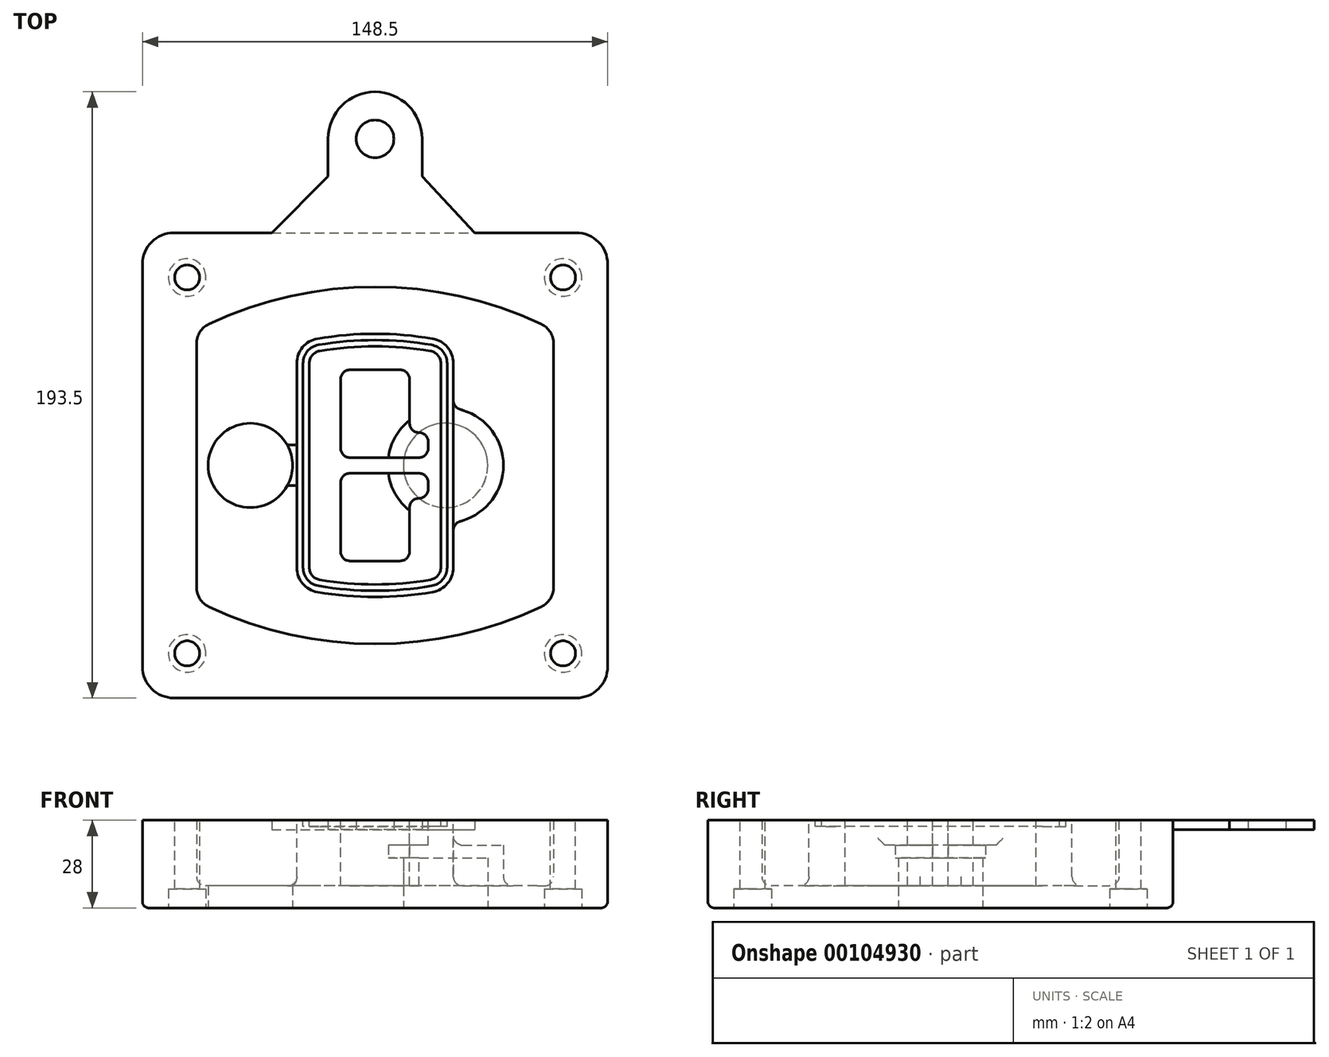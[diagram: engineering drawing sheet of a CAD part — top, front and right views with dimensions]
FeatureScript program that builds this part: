
annotation { "Feature Type Name" : "Feature", "Feature Type Description" : "" }
export const myFeature = defineFeature(function(context is Context, id is Id, definition is map)
    precondition{}
    {
        {
            var Q0;
            Q0=qCreatedBy(makeId("Top.planeOp"),FACE);
            var sketch = newSketch(context, id + "F0", { "sketchPlane" : qUnion([Q0])});
            skPoint(sketch, "E0.rect.middle", {"position": v(0, 0) * mm});
            skLineSegment(sketch, "E1.bottom", {"start": v(-64.25, -74.25) * mm, "end": v(64.25, -74.25) * mm});
            skLineSegment(sketch, "E1.top", {"start": v(-64.25, 74.25) * mm, "end": v(64.25, 74.25) * mm});
            skLineSegment(sketch, "E1.left", {"start": v(-74.25, -64.25) * mm, "end": v(-74.25, 64.25) * mm});
            skLineSegment(sketch, "E1.right", {"start": v(74.25, -64.25) * mm, "end": v(74.25, 64.25) * mm});
            skLineSegment(sketch, "E2", {"start": v(-74.25, 74.25) * mm, "end": v(74.25, -74.25) * mm, "construction": true});
            skLineSegment(sketch, "E3", {"start": v(74.25, 74.25) * mm, "end": v(-74.25, -74.25) * mm, "construction": true});
            skCircle(sketch, "E4", {"center": v(-60, 60) * mm, "radius": 4 * mm});
            skCircle(sketch, "E5", {"center": v(60, 60) * mm, "radius": 4 * mm});
            skCircle(sketch, "E6", {"center": v(60, -60) * mm, "radius": 4 * mm});
            skCircle(sketch, "E7", {"center": v(-60, -60) * mm, "radius": 4 * mm});
            skLineSegment(sketch, "E8", {"start": v(-60, 60) * mm, "end": v(60, 60) * mm, "construction": true});
            skLineSegment(sketch, "E9", {"start": v(60, 60) * mm, "end": v(60, -60) * mm, "construction": true});
            skLineSegment(sketch, "E10", {"start": v(60, -60) * mm, "end": v(-60, -60) * mm, "construction": true});
            skLineSegment(sketch, "E11", {"start": v(-60, -60) * mm, "end": v(-60, 60) * mm, "construction": true});
            skLineSegment(sketch, "E12", {"start": v(-60, 38.83) * mm, "end": v(-60, -38.83) * mm});
            skLineSegment(sketch, "E13", {"start": v(60, 38.83) * mm, "end": v(60, -38.83) * mm});
            skArc(sketch, "E14", {"start": v(54.26, 47.88) * mm, "mid": v(0, 60) * mm, "end": v(-54.26, 47.88) * mm});
            skArc(sketch, "E15", {"start": v(-54.26, -47.88) * mm, "mid": v(0, -60) * mm, "end": v(54.26, -47.88) * mm});
            skLineSegment(sketch, "E16", {"start": v(-60, 0) * mm, "end": v(60, 0) * mm, "construction": true});
            skPoint(sketch, "E17.visualSharp", {"position": v(-60, -45) * mm});
            skArc(sketch, "E17.filletArc", {"start": v(-60, -38.83) * mm, "mid": v(-58.44, -44.2) * mm, "end": v(-54.26, -47.88) * mm});
            skPoint(sketch, "E18.visualSharp", {"position": v(-60, 45) * mm});
            skArc(sketch, "E18.filletArc", {"start": v(-54.26, 47.88) * mm, "mid": v(-58.44, 44.2) * mm, "end": v(-60, 38.83) * mm});
            skPoint(sketch, "E19.visualSharp", {"position": v(60, 45) * mm});
            skArc(sketch, "E19.filletArc", {"start": v(60, 38.83) * mm, "mid": v(58.44, 44.2) * mm, "end": v(54.26, 47.88) * mm});
            skPoint(sketch, "E20.visualSharp", {"position": v(60, -45) * mm});
            skArc(sketch, "E20.filletArc", {"start": v(54.26, -47.88) * mm, "mid": v(58.44, -44.2) * mm, "end": v(60, -38.83) * mm});
            skPoint(sketch, "E21.visualSharp", {"position": v(-74.25, 74.25) * mm});
            skArc(sketch, "E21.filletArc", {"start": v(-64.25, 74.25) * mm, "mid": v(-71.32, 71.32) * mm, "end": v(-74.25, 64.25) * mm});
            skPoint(sketch, "E22.visualSharp", {"position": v(74.25, 74.25) * mm});
            skArc(sketch, "E22.filletArc", {"start": v(74.25, 64.25) * mm, "mid": v(71.32, 71.32) * mm, "end": v(64.25, 74.25) * mm});
            skPoint(sketch, "E23.visualSharp", {"position": v(74.25, -74.25) * mm});
            skArc(sketch, "E23.filletArc", {"start": v(64.25, -74.25) * mm, "mid": v(71.32, -71.32) * mm, "end": v(74.25, -64.25) * mm});
            skPoint(sketch, "E24.visualSharp", {"position": v(-74.25, -74.25) * mm});
            skArc(sketch, "E24.filletArc", {"start": v(-74.25, -64.25) * mm, "mid": v(-71.32, -71.32) * mm, "end": v(-64.25, -74.25) * mm});
            skArc(sketch, "E25.0", {"start": v(57, 38.83) * mm, "mid": v(55.9, 42.58) * mm, "end": v(52.98, 45.17) * mm});
            skLineSegment(sketch, "E25.1", {"start": v(57, 38.83) * mm, "end": v(57, -38.83) * mm});
            skArc(sketch, "E25.2", {"start": v(52.98, -45.17) * mm, "mid": v(55.9, -42.58) * mm, "end": v(57, -38.83) * mm});
            skArc(sketch, "E25.3", {"start": v(-52.98, -45.17) * mm, "mid": v(0, -57) * mm, "end": v(52.98, -45.17) * mm});
            skArc(sketch, "E25.4", {"start": v(-57, -38.83) * mm, "mid": v(-55.9, -42.58) * mm, "end": v(-52.98, -45.17) * mm});
            skArc(sketch, "E25.5", {"start": v(52.98, 45.17) * mm, "mid": v(0, 57) * mm, "end": v(-52.98, 45.17) * mm});
            skLineSegment(sketch, "E25.6", {"start": v(-57, 38.83) * mm, "end": v(-57, -38.83) * mm});
            skArc(sketch, "E25.7", {"start": v(-52.98, 45.17) * mm, "mid": v(-55.9, 42.58) * mm, "end": v(-57, 38.83) * mm});
            skArc(sketch, "E26.0", {"start": v(-55.96, 51.5) * mm, "mid": v(-61.82, 46.33) * mm, "end": v(-64, 38.83) * mm});
            skArc(sketch, "E26.1", {"start": v(55.96, 51.5) * mm, "mid": v(0, 64) * mm, "end": v(-55.96, 51.5) * mm});
            skArc(sketch, "E26.2", {"start": v(64, 38.83) * mm, "mid": v(61.82, 46.33) * mm, "end": v(55.96, 51.5) * mm});
            skLineSegment(sketch, "E26.3", {"start": v(64, 38.83) * mm, "end": v(64, -38.83) * mm});
            skArc(sketch, "E26.4", {"start": v(55.96, -51.5) * mm, "mid": v(61.82, -46.33) * mm, "end": v(64, -38.83) * mm});
            skLineSegment(sketch, "E26.5", {"start": v(-64, 38.83) * mm, "end": v(-64, -38.83) * mm});
            skArc(sketch, "E26.6", {"start": v(-55.96, -51.5) * mm, "mid": v(0, -64) * mm, "end": v(55.96, -51.5) * mm});
            skArc(sketch, "E26.7", {"start": v(-64, -38.83) * mm, "mid": v(-61.82, -46.33) * mm, "end": v(-55.96, -51.5) * mm});
            skSolve(sketch);
        }
        {
            var Q0;
            Q0=makeQuery(id+"F0.imprint","IMPRINT",FACE,{"disambiguationData":[TD([[makeQuery(id+"F0.imprint","IMPRINT",EDGE,{"derivedFrom":sQuery(id+"F0.wireOp",EDGE,"E1.bottom")}),1.0]])]});
            var Q1;
            Q1=makeQuery(id+"F0.imprint","IMPRINT",FACE,{"disambiguationData":[TD([[makeQuery(id+"F0.imprint","IMPRINT",EDGE,{"derivedFrom":sQuery(id+"F0.wireOp",EDGE,"E12")}),1.0]])]});
            var Q2;
            Q2=makeQuery(id+"F0.imprint","IMPRINT",FACE,{"disambiguationData":[TD([[makeQuery(id+"F0.imprint","IMPRINT",EDGE,{"derivedFrom":sQuery(id+"F0.wireOp",EDGE,"E25.0")}),1.0]])]});
            var Q3;
            Q3=makeQuery(id+"F0.imprint","IMPRINT",FACE,{"disambiguationData":[TD([[makeQuery(id+"F0.imprint","IMPRINT",EDGE,{"derivedFrom":sQuery(id+"F0.wireOp",EDGE,"E12")}),-1.0]])]});
            extrude(context, id + "F1", {"entities" : qUnion([Q0, Q1, Q2, Q3]), "oppositeDirection" : true, "depth" : 25 * mm});
        }
        {
            var Q0;
            Q0=makeQuery(id+"F0.imprint","IMPRINT",FACE,{"disambiguationData":[TD([[makeQuery(id+"F0.imprint","IMPRINT",EDGE,{"derivedFrom":sQuery(id+"F0.wireOp",EDGE,"E12")}),1.0]])]});
            extrude(context, id + "F2", {"entities" : qUnion([Q0]), "operationType" : NewBodyOperationType.ADD, "depth" : 3 * mm});
        }
        {
            var Q0;
            Q0=makeQuery(id+"F0.imprint","IMPRINT",FACE,{"disambiguationData":[TD([[makeQuery(id+"F0.imprint","IMPRINT",EDGE,{"derivedFrom":sQuery(id+"F0.wireOp",EDGE,"E25.0")}),1.0]])]});
            extrude(context, id + "F3", {"entities" : qUnion([Q0]), "operationType" : NewBodyOperationType.REMOVE, "oppositeDirection" : true, "depth" : 18 * mm});
        }
        {
            var Q0;
            Q0=makeQuery(id+"F2.opExtrude","CAP_FACE",FACE,{"disambiguationData":[OSD([sQuery(id+"F0.wireOp",EDGE,"E12"),sQuery(id+"F0.wireOp",EDGE,"E13"),sQuery(id+"F0.wireOp",EDGE,"E14"),sQuery(id+"F0.wireOp",EDGE,"E15"),sQuery(id+"F0.wireOp",EDGE,"E17.filletArc"),sQuery(id+"F0.wireOp",EDGE,"E18.filletArc"),sQuery(id+"F0.wireOp",EDGE,"E19.filletArc"),sQuery(id+"F0.wireOp",EDGE,"E20.filletArc"),sQuery(id+"F0.wireOp",EDGE,"E25.0"),sQuery(id+"F0.wireOp",EDGE,"E25.1"),sQuery(id+"F0.wireOp",EDGE,"E25.2"),sQuery(id+"F0.wireOp",EDGE,"E25.3"),sQuery(id+"F0.wireOp",EDGE,"E25.4"),sQuery(id+"F0.wireOp",EDGE,"E25.5"),sQuery(id+"F0.wireOp",EDGE,"E25.6"),sQuery(id+"F0.wireOp",EDGE,"E25.7")])],"isStart":false});
            var sketch = newSketch(context, id + "F4", { "sketchPlane" : qUnion([Q0])});
            skArc(sketch, "E27.0", {"start": v(-18.34, -40.45) * mm, "mid": v(0, -42) * mm, "end": v(18.34, -40.45) * mm});
            skArc(sketch, "E28.0", {"start": v(18.34, 40.45) * mm, "mid": v(0, 42) * mm, "end": v(-18.34, 40.45) * mm});
            skLineSegment(sketch, "E29", {"start": v(-25, 32.57) * mm, "end": v(-25, -32.57) * mm});
            skLineSegment(sketch, "E30", {"start": v(25, 32.57) * mm, "end": v(25, -32.57) * mm});
            skLineSegment(sketch, "E31", {"start": v(-25, 39.1) * mm, "end": v(25, 39.1) * mm, "construction": true});
            skLineSegment(sketch, "E32", {"start": v(-25, -39.1) * mm, "end": v(25, -39.1) * mm, "construction": true});
            skPoint(sketch, "E33.visualSharp", {"position": v(-25, 39.1) * mm});
            skArc(sketch, "E33.filletArc", {"start": v(-18.34, 40.45) * mm, "mid": v(-23.11, 37.73) * mm, "end": v(-25, 32.57) * mm});
            skPoint(sketch, "E34.visualSharp", {"position": v(25, 39.1) * mm});
            skArc(sketch, "E34.filletArc", {"start": v(25, 32.57) * mm, "mid": v(23.11, 37.73) * mm, "end": v(18.34, 40.45) * mm});
            skPoint(sketch, "E35.visualSharp", {"position": v(25, -39.1) * mm});
            skArc(sketch, "E35.filletArc", {"start": v(18.34, -40.45) * mm, "mid": v(23.11, -37.73) * mm, "end": v(25, -32.57) * mm});
            skPoint(sketch, "E36.visualSharp", {"position": v(-25, -39.1) * mm});
            skArc(sketch, "E36.filletArc", {"start": v(-25, -32.57) * mm, "mid": v(-23.11, -37.73) * mm, "end": v(-18.34, -40.45) * mm});
            skArc(sketch, "E37.0", {"start": v(52.98, 45.17) * mm, "mid": v(0, 57) * mm, "end": v(-52.98, 45.17) * mm});
            skArc(sketch, "E37.1", {"start": v(-52.98, 45.17) * mm, "mid": v(-55.9, 42.58) * mm, "end": v(-57, 38.83) * mm});
            skLineSegment(sketch, "E37.2", {"start": v(-57, 38.83) * mm, "end": v(-57, -38.83) * mm});
            skArc(sketch, "E37.3", {"start": v(-57, -38.83) * mm, "mid": v(-55.9, -42.58) * mm, "end": v(-52.98, -45.17) * mm});
            skArc(sketch, "E37.4", {"start": v(-52.98, -45.17) * mm, "mid": v(0, -57) * mm, "end": v(52.98, -45.17) * mm});
            skArc(sketch, "E37.5", {"start": v(52.98, -45.17) * mm, "mid": v(55.9, -42.58) * mm, "end": v(57, -38.83) * mm});
            skLineSegment(sketch, "E37.6", {"start": v(57, 38.83) * mm, "end": v(57, -38.83) * mm});
            skArc(sketch, "E37.7", {"start": v(57, 38.83) * mm, "mid": v(55.9, 42.58) * mm, "end": v(52.98, 45.17) * mm});
            skLineSegment(sketch, "E38.0", {"start": v(23, 32.57) * mm, "end": v(23, -32.57) * mm});
            skArc(sketch, "E38.1", {"start": v(18, -38.48) * mm, "mid": v(21.58, -36.44) * mm, "end": v(23, -32.57) * mm});
            skArc(sketch, "E38.2", {"start": v(-18, -38.48) * mm, "mid": v(0, -40) * mm, "end": v(18, -38.48) * mm});
            skArc(sketch, "E38.3", {"start": v(-23, -32.57) * mm, "mid": v(-21.58, -36.44) * mm, "end": v(-18, -38.48) * mm});
            skLineSegment(sketch, "E38.4", {"start": v(-23, 32.57) * mm, "end": v(-23, -32.57) * mm});
            skArc(sketch, "E38.5", {"start": v(23, 32.57) * mm, "mid": v(21.58, 36.44) * mm, "end": v(18, 38.48) * mm});
            skArc(sketch, "E38.6", {"start": v(-18, 38.48) * mm, "mid": v(-21.58, 36.44) * mm, "end": v(-23, 32.57) * mm});
            skArc(sketch, "E38.7", {"start": v(18, 38.48) * mm, "mid": v(0, 40) * mm, "end": v(-18, 38.48) * mm});
            skArc(sketch, "E39.0", {"start": v(21, 32.57) * mm, "mid": v(20.06, 35.15) * mm, "end": v(17.67, 36.5) * mm});
            skLineSegment(sketch, "E39.1", {"start": v(21, 32.57) * mm, "end": v(21, -32.57) * mm});
            skArc(sketch, "E39.2", {"start": v(17.67, -36.5) * mm, "mid": v(20.06, -35.15) * mm, "end": v(21, -32.57) * mm});
            skArc(sketch, "E39.3", {"start": v(-17.67, -36.5) * mm, "mid": v(0, -38) * mm, "end": v(17.67, -36.5) * mm});
            skArc(sketch, "E39.4", {"start": v(-21, -32.57) * mm, "mid": v(-20.06, -35.15) * mm, "end": v(-17.67, -36.5) * mm});
            skArc(sketch, "E39.5", {"start": v(17.67, 36.5) * mm, "mid": v(0, 38) * mm, "end": v(-17.67, 36.5) * mm});
            skLineSegment(sketch, "E39.6", {"start": v(-21, 32.57) * mm, "end": v(-21, -32.57) * mm});
            skArc(sketch, "E39.7", {"start": v(-17.67, 36.5) * mm, "mid": v(-20.06, 35.15) * mm, "end": v(-21, 32.57) * mm});
            skLineSegment(sketch, "E40", {"start": v(-25, 0) * mm, "end": v(25, 0) * mm, "construction": true});
            skLineSegment(sketch, "E41", {"start": v(-11, 5.5) * mm, "end": v(-11, 27.5) * mm});
            skLineSegment(sketch, "E42", {"start": v(-8, 30.5) * mm, "end": v(8, 30.5) * mm});
            skLineSegment(sketch, "E43", {"start": v(11, 27.5) * mm, "end": v(11, 13.5) * mm});
            skLineSegment(sketch, "E44", {"start": v(14, 10.5) * mm, "end": v(14, 10.5) * mm});
            skLineSegment(sketch, "E45", {"start": v(17, 7.5) * mm, "end": v(17, 5.5) * mm});
            skLineSegment(sketch, "E46", {"start": v(14, 2.5) * mm, "end": v(-8, 2.5) * mm});
            skPoint(sketch, "E47.visualSharp", {"position": v(-11, 30.5) * mm});
            skArc(sketch, "E47.filletArc", {"start": v(-8, 30.5) * mm, "mid": v(-10.12, 29.62) * mm, "end": v(-11, 27.5) * mm});
            skPoint(sketch, "E48.visualSharp", {"position": v(11, 30.5) * mm});
            skArc(sketch, "E48.filletArc", {"start": v(11, 27.5) * mm, "mid": v(10.12, 29.62) * mm, "end": v(8, 30.5) * mm});
            skPoint(sketch, "E49.visualSharp", {"position": v(11, 10.5) * mm});
            skArc(sketch, "E49.filletArc", {"start": v(11, 13.5) * mm, "mid": v(11.88, 11.38) * mm, "end": v(14, 10.5) * mm});
            skPoint(sketch, "E50.visualSharp", {"position": v(17, 10.5) * mm});
            skArc(sketch, "E50.filletArc", {"start": v(17, 7.5) * mm, "mid": v(16.12, 9.62) * mm, "end": v(14, 10.5) * mm});
            skPoint(sketch, "E51.visualSharp", {"position": v(17, 2.5) * mm});
            skArc(sketch, "E51.filletArc", {"start": v(14, 2.5) * mm, "mid": v(16.12, 3.38) * mm, "end": v(17, 5.5) * mm});
            skPoint(sketch, "E52.visualSharp", {"position": v(-11, 2.5) * mm});
            skArc(sketch, "E52.filletArc", {"start": v(-11, 5.5) * mm, "mid": v(-10.12, 3.38) * mm, "end": v(-8, 2.5) * mm});
            skLineSegment(sketch, "E53.0.MirrorCS", {"start": v(14, -2.5) * mm, "end": v(-8, -2.5) * mm});
            skArc(sketch, "E54.0.MirrorCS", {"start": v(-11, -5.5) * mm, "mid": v(-10.12, -3.38) * mm, "end": v(-8, -2.5) * mm});
            skLineSegment(sketch, "E55.0.MirrorCS", {"start": v(-11, -5.5) * mm, "end": v(-11, -27.5) * mm});
            skArc(sketch, "E56.0.MirrorCS", {"start": v(-8, -30.5) * mm, "mid": v(-10.12, -29.62) * mm, "end": v(-11, -27.5) * mm});
            skLineSegment(sketch, "E57.0.MirrorCS", {"start": v(-8, -30.5) * mm, "end": v(8, -30.5) * mm});
            skArc(sketch, "E58.0.MirrorCS", {"start": v(11, -27.5) * mm, "mid": v(10.12, -29.62) * mm, "end": v(8, -30.5) * mm});
            skLineSegment(sketch, "E59.0.MirrorCS", {"start": v(11, -27.5) * mm, "end": v(11, -13.5) * mm});
            skArc(sketch, "E60.0.MirrorCS", {"start": v(11, -13.5) * mm, "mid": v(11.88, -11.38) * mm, "end": v(14, -10.5) * mm});
            skArc(sketch, "E61.0.MirrorCS", {"start": v(17, -7.5) * mm, "mid": v(16.12, -9.62) * mm, "end": v(14, -10.5) * mm});
            skLineSegment(sketch, "E62.0.MirrorCS", {"start": v(17, -7.5) * mm, "end": v(17, -5.5) * mm});
            skArc(sketch, "E63.0.MirrorCS", {"start": v(14, -2.5) * mm, "mid": v(16.12, -3.38) * mm, "end": v(17, -5.5) * mm});
            skSolve(sketch);
        }
        {
            var Q0;
            Q0=makeQuery(id+"F4.imprint","IMPRINT",FACE,{"disambiguationData":[TD([[makeQuery(id+"F4.imprint","IMPRINT",EDGE,{"derivedFrom":sQuery(id+"F4.wireOp",EDGE,"E27.0")}),1.0]])]});
            var Q1;
            Q1=makeQuery(id+"F4.imprint","IMPRINT",FACE,{"disambiguationData":[TD([[makeQuery(id+"F4.imprint","IMPRINT",EDGE,{"derivedFrom":sQuery(id+"F4.wireOp",EDGE,"E38.0")}),-1.0]])]});
            var Q2;
            Q2=makeQuery(id+"F4.imprint","IMPRINT",FACE,{"disambiguationData":[TD([[makeQuery(id+"F4.imprint","IMPRINT",EDGE,{"derivedFrom":sQuery(id+"F4.wireOp",EDGE,"E39.0")}),1.0]])]});
            extrude(context, id + "F5", {"entities" : qUnion([Q0, Q1, Q2]), "operationType" : NewBodyOperationType.ADD, "endBound" : BoundingType.UP_TO_NEXT, "oppositeDirection" : true, "depth" : 25 * mm});
        }
        {
            var Q0;
            Q0=makeQuery(id+"F4.imprint","IMPRINT",FACE,{"disambiguationData":[TD([[makeQuery(id+"F4.imprint","IMPRINT",EDGE,{"derivedFrom":sQuery(id+"F4.wireOp",EDGE,"E38.0")}),-1.0]])]});
            extrude(context, id + "F6", {"entities" : qUnion([Q0]), "operationType" : NewBodyOperationType.REMOVE, "oppositeDirection" : true, "depth" : 2 * mm});
        }
        {
            var Q0;
            Q0=makeQuery(id+"F1.opExtrude","CAP_FACE",FACE,{"disambiguationData":[OSD([sQuery(id+"F0.wireOp",EDGE,"E1.bottom"),sQuery(id+"F0.wireOp",EDGE,"E1.top"),sQuery(id+"F0.wireOp",EDGE,"E1.left"),sQuery(id+"F0.wireOp",EDGE,"E1.right"),sQuery(id+"F0.wireOp",EDGE,"E4"),sQuery(id+"F0.wireOp",EDGE,"E5"),sQuery(id+"F0.wireOp",EDGE,"E6"),sQuery(id+"F0.wireOp",EDGE,"E7"),sQuery(id+"F0.wireOp",EDGE,"E21.filletArc"),sQuery(id+"F0.wireOp",EDGE,"E22.filletArc"),sQuery(id+"F0.wireOp",EDGE,"E23.filletArc"),sQuery(id+"F0.wireOp",EDGE,"E24.filletArc")])],"isStart":false});
            var sketch = newSketch(context, id + "F7", { "sketchPlane" : qUnion([Q0])});
            skCircle(sketch, "E64", {"center": v(22.5, 0) * mm, "radius": 13.47 * mm});
            skCircle(sketch, "E65", {"center": v(-39.81, 0) * mm, "radius": 13.47 * mm});
            skLineSegment(sketch, "E66", {"start": v(74.25, 0) * mm, "end": v(-74.25, 0) * mm});
            skCircle(sketch, "E67", {"center": v(22.5, 0) * mm, "radius": 18.47 * mm});
            skCircle(sketch, "E68", {"center": v(60, -60) * mm, "radius": 6 * mm});
            skCircle(sketch, "E69", {"center": v(-60, -60) * mm, "radius": 6 * mm});
            skCircle(sketch, "E70", {"center": v(-60, 60) * mm, "radius": 6 * mm});
            skCircle(sketch, "E71", {"center": v(60, 60) * mm, "radius": 6 * mm});
            skSolve(sketch);
        }
        {
            var Q0;
            {var subQ1=sQuery(id+"F7.wireOp",EDGE,"E66");var subQ4=sQuery(id+"F7.wireOp",EDGE,"E64");var subQ6=makeQuery(id+"F7.imprint","INTERSECT",VERTEX,{"disambiguationData":[OD(0.0)],"derivedFrom":[subQ4,subQ1]});Q0=makeQuery(id+"F7.imprint","IMPRINT",FACE,{"disambiguationData":[TD([[makeQuery(id+"F7.imprint","IMPRINT",EDGE,{"disambiguationData":[TD([[subQ6,-1.0]])],"derivedFrom":subQ4}),-1.0]])]});}
            var Q1;
            {var subQ0=sQuery(id+"F7.wireOp",EDGE,"E66");var subQ1=sQuery(id+"F7.wireOp",EDGE,"E64");var subQ3=makeQuery(id+"F7.imprint","INTERSECT",VERTEX,{"disambiguationData":[OD(0.0)],"derivedFrom":[subQ1,subQ0]});Q1=makeQuery(id+"F7.imprint","IMPRINT",FACE,{"disambiguationData":[TD([[makeQuery(id+"F7.imprint","IMPRINT",EDGE,{"disambiguationData":[TD([[subQ3,-1.0]])],"derivedFrom":subQ1}),1.0]])]});}
            var Q2;
            {var subQ0=sQuery(id+"F7.wireOp",EDGE,"E66");var subQ1=sQuery(id+"F7.wireOp",EDGE,"E64");var subQ3=makeQuery(id+"F7.imprint","INTERSECT",VERTEX,{"disambiguationData":[OD(0.0)],"derivedFrom":[subQ1,subQ0]});Q2=makeQuery(id+"F7.imprint","IMPRINT",FACE,{"disambiguationData":[TD([[makeQuery(id+"F7.imprint","IMPRINT",EDGE,{"disambiguationData":[TD([[subQ3,1.0]])],"derivedFrom":subQ1}),1.0]])]});}
            var Q3;
            {var subQ1=sQuery(id+"F7.wireOp",EDGE,"E66");var subQ4=sQuery(id+"F7.wireOp",EDGE,"E64");var subQ6=makeQuery(id+"F7.imprint","INTERSECT",VERTEX,{"disambiguationData":[OD(0.0)],"derivedFrom":[subQ4,subQ1]});Q3=makeQuery(id+"F7.imprint","IMPRINT",FACE,{"disambiguationData":[TD([[makeQuery(id+"F7.imprint","IMPRINT",EDGE,{"disambiguationData":[TD([[subQ6,1.0]])],"derivedFrom":subQ4}),-1.0]])]});}
            extrude(context, id + "F8", {"entities" : qUnion([Q0, Q1, Q2, Q3]), "operationType" : NewBodyOperationType.ADD, "oppositeDirection" : true, "depth" : 20 * mm});
        }
        {
            var Q0;
            {var subQ0=sQuery(id+"F7.wireOp",EDGE,"E66");var subQ1=sQuery(id+"F7.wireOp",EDGE,"E64");var subQ3=makeQuery(id+"F7.imprint","INTERSECT",VERTEX,{"disambiguationData":[OD(0.0)],"derivedFrom":[subQ1,subQ0]});Q0=makeQuery(id+"F7.imprint","IMPRINT",FACE,{"disambiguationData":[TD([[makeQuery(id+"F7.imprint","IMPRINT",EDGE,{"disambiguationData":[TD([[subQ3,-1.0]])],"derivedFrom":subQ1}),1.0]])]});}
            var Q1;
            {var subQ0=sQuery(id+"F7.wireOp",EDGE,"E66");var subQ1=sQuery(id+"F7.wireOp",EDGE,"E64");var subQ3=makeQuery(id+"F7.imprint","INTERSECT",VERTEX,{"disambiguationData":[OD(0.0)],"derivedFrom":[subQ1,subQ0]});Q1=makeQuery(id+"F7.imprint","IMPRINT",FACE,{"disambiguationData":[TD([[makeQuery(id+"F7.imprint","IMPRINT",EDGE,{"disambiguationData":[TD([[subQ3,1.0]])],"derivedFrom":subQ1}),1.0]])]});}
            extrude(context, id + "F9", {"entities" : qUnion([Q0, Q1]), "operationType" : NewBodyOperationType.REMOVE, "oppositeDirection" : true, "depth" : 16 * mm});
        }
        {
            var Q0;
            {var subQ0=sQuery(id+"F7.wireOp",EDGE,"E66");var subQ1=sQuery(id+"F7.wireOp",EDGE,"E65");var subQ3=makeQuery(id+"F7.imprint","INTERSECT",VERTEX,{"disambiguationData":[OD(0.0)],"derivedFrom":[subQ1,subQ0]});Q0=makeQuery(id+"F7.imprint","IMPRINT",FACE,{"disambiguationData":[TD([[makeQuery(id+"F7.imprint","IMPRINT",EDGE,{"disambiguationData":[TD([[subQ3,-1.0]])],"derivedFrom":subQ1}),1.0]])]});}
            var Q1;
            {var subQ0=sQuery(id+"F7.wireOp",EDGE,"E66");var subQ1=sQuery(id+"F7.wireOp",EDGE,"E65");var subQ3=makeQuery(id+"F7.imprint","INTERSECT",VERTEX,{"disambiguationData":[OD(0.0)],"derivedFrom":[subQ1,subQ0]});Q1=makeQuery(id+"F7.imprint","IMPRINT",FACE,{"disambiguationData":[TD([[makeQuery(id+"F7.imprint","IMPRINT",EDGE,{"disambiguationData":[TD([[subQ3,1.0]])],"derivedFrom":subQ1}),1.0]])]});}
            extrude(context, id + "F10", {"entities" : qUnion([Q0, Q1]), "operationType" : NewBodyOperationType.REMOVE, "oppositeDirection" : true, "depth" : 25 * mm});
        }
        {
            var Q0;
            Q0=makeQuery(id+"F7.imprint","IMPRINT",FACE,{"disambiguationData":[TD([[makeQuery(id+"F7.imprint","IMPRINT",EDGE,{"derivedFrom":sQuery(id+"F7.wireOp",EDGE,"E68")}),1.0]])]});
            var Q1;
            Q1=makeQuery(id+"F7.imprint","IMPRINT",FACE,{"disambiguationData":[TD([[makeQuery(id+"F7.imprint","IMPRINT",EDGE,{"derivedFrom":makeQuery(id+"F1.opExtrude","CAP_EDGE",EDGE,{"disambiguationData":[OSD([sQuery(id+"F0.wireOp",EDGE,"E5")])],"isStart":false})}),-1.0]])]});
            var Q2;
            Q2=makeQuery(id+"F7.imprint","IMPRINT",FACE,{"disambiguationData":[TD([[makeQuery(id+"F7.imprint","IMPRINT",EDGE,{"derivedFrom":sQuery(id+"F7.wireOp",EDGE,"E69")}),1.0]])]});
            var Q3;
            Q3=makeQuery(id+"F7.imprint","IMPRINT",FACE,{"disambiguationData":[TD([[makeQuery(id+"F7.imprint","IMPRINT",EDGE,{"derivedFrom":makeQuery(id+"F1.opExtrude","CAP_EDGE",EDGE,{"disambiguationData":[OSD([sQuery(id+"F0.wireOp",EDGE,"E4")])],"isStart":false})}),-1.0]])]});
            var Q4;
            Q4=makeQuery(id+"F7.imprint","IMPRINT",FACE,{"disambiguationData":[TD([[makeQuery(id+"F7.imprint","IMPRINT",EDGE,{"derivedFrom":sQuery(id+"F7.wireOp",EDGE,"E70")}),1.0]])]});
            var Q5;
            Q5=makeQuery(id+"F7.imprint","IMPRINT",FACE,{"disambiguationData":[TD([[makeQuery(id+"F7.imprint","IMPRINT",EDGE,{"derivedFrom":makeQuery(id+"F1.opExtrude","CAP_EDGE",EDGE,{"disambiguationData":[OSD([sQuery(id+"F0.wireOp",EDGE,"E7")])],"isStart":false})}),-1.0]])]});
            var Q6;
            Q6=makeQuery(id+"F7.imprint","IMPRINT",FACE,{"disambiguationData":[TD([[makeQuery(id+"F7.imprint","IMPRINT",EDGE,{"derivedFrom":sQuery(id+"F7.wireOp",EDGE,"E71")}),1.0]])]});
            var Q7;
            Q7=makeQuery(id+"F7.imprint","IMPRINT",FACE,{"disambiguationData":[TD([[makeQuery(id+"F7.imprint","IMPRINT",EDGE,{"derivedFrom":makeQuery(id+"F1.opExtrude","CAP_EDGE",EDGE,{"disambiguationData":[OSD([sQuery(id+"F0.wireOp",EDGE,"E6")])],"isStart":false})}),-1.0]])]});
            extrude(context, id + "F11", {"entities" : qUnion([Q0, Q1, Q2, Q3, Q4, Q5, Q6, Q7]), "operationType" : NewBodyOperationType.REMOVE, "oppositeDirection" : true, "depth" : 6 * mm});
        }
        {
            var Q0;
            Q0=makeQuery(id+"F9.boolean.opBoolean","COPY",FACE,{"derivedFrom":makeQuery(id+"F9.opExtrude","CAP_FACE",FACE,{"disambiguationData":[OSD([sQuery(id+"F7.wireOp",EDGE,"E64")])],"isStart":false})});
            var sketch = newSketch(context, id + "F12", { "sketchPlane" : qUnion([Q0])});
            skArc(sketch, "E72.0", {"start": v(11, 14.45) * mm, "mid": v(6.45, 9.13) * mm, "end": v(4.2, 2.5) * mm});
            skArc(sketch, "E72.1", {"start": v(4.2, -2.5) * mm, "mid": v(6.45, -9.13) * mm, "end": v(11, -14.45) * mm});
            skLineSegment(sketch, "E73", {"start": v(4.2, -2.5) * mm, "end": v(14, -2.5) * mm});
            skLineSegment(sketch, "E74.0", {"start": v(14, 2.5) * mm, "end": v(4.2, 2.5) * mm});
            skArc(sketch, "E74.1", {"start": v(14, 2.5) * mm, "mid": v(16.12, 3.38) * mm, "end": v(17, 5.5) * mm});
            skLineSegment(sketch, "E74.2", {"start": v(17, 7.5) * mm, "end": v(17, 5.5) * mm});
            skArc(sketch, "E74.3", {"start": v(17, 7.5) * mm, "mid": v(16.12, 9.62) * mm, "end": v(14, 10.5) * mm});
            skArc(sketch, "E74.4", {"start": v(11, 13.5) * mm, "mid": v(11.88, 11.38) * mm, "end": v(14, 10.5) * mm});
            skLineSegment(sketch, "E74.5", {"start": v(11, 14.45) * mm, "end": v(11, 13.5) * mm});
            skLineSegment(sketch, "E74.7", {"start": v(14, -2.5) * mm, "end": v(4.2, -2.5) * mm});
            skArc(sketch, "E74.8", {"start": v(14, -2.5) * mm, "mid": v(16.12, -3.38) * mm, "end": v(17, -5.5) * mm});
            skLineSegment(sketch, "E74.9", {"start": v(17, -7.5) * mm, "end": v(17, -5.5) * mm});
            skArc(sketch, "E74.10", {"start": v(17, -7.5) * mm, "mid": v(16.12, -9.62) * mm, "end": v(14, -10.5) * mm});
            skArc(sketch, "E74.11", {"start": v(11, -13.5) * mm, "mid": v(11.88, -11.38) * mm, "end": v(14, -10.5) * mm});
            skLineSegment(sketch, "E74.12", {"start": v(11, -14.45) * mm, "end": v(11, -13.5) * mm});
            skPoint(sketch, "E75.orphan", {"position": v(11, -27.5) * mm});
            skPoint(sketch, "E76.orphan", {"position": v(-8, -2.5) * mm});
            skPoint(sketch, "E77.orphan", {"position": v(-8, 2.5) * mm});
            skPoint(sketch, "E78.orphan", {"position": v(11, 27.5) * mm});
            skSolve(sketch);
        }
        {
            var Q0;
            {var subQ7=sQuery(id+"F12.wireOp",EDGE,"E72.0");var subQ14=sQuery(id+"F12.wireOp",EDGE,"E72.1");var subQ16=sQuery(id+"F12.wireOp",EDGE,"E74.1");var subQ18=sQuery(id+"F12.wireOp",EDGE,"E74.8");Q0=qUnion([makeQuery(id+"F12.imprint","IMPRINT",FACE,{"disambiguationData":[TD([[makeQuery(id+"F12.imprint","IMPRINT",EDGE,{"derivedFrom":subQ7}),1.0]])]}),makeQuery(id+"F12.imprint","IMPRINT",FACE,{"disambiguationData":[TD([[makeQuery(id+"F12.imprint","IMPRINT",EDGE,{"derivedFrom":subQ14}),1.0]])]}),makeQuery(id+"F12.imprint","IMPRINT",FACE,{"disambiguationData":[TD([[makeQuery(id+"F12.imprint","IMPRINT",EDGE,{"derivedFrom":subQ16}),1.0]])]}),makeQuery(id+"F12.imprint","IMPRINT",FACE,{"disambiguationData":[TD([[makeQuery(id+"F12.imprint","IMPRINT",EDGE,{"derivedFrom":subQ18}),-1.0]])]})]);}
            var Q1;
            Q1=makeQuery(id+"F5.boolean.opBoolean","SPLIT",FACE,{"disambiguationData":[TD([makeQuery(id+"F5.opExtrude","SWEPT_FACE",FACE,{"disambiguationData":[OSD([sQuery(id+"F4.wireOp",EDGE,"E41")])]})])],"derivedFrom":makeQuery(id+"F3.boolean.opBoolean","COPY",FACE,{"derivedFrom":makeQuery(id+"F3.opExtrude","CAP_FACE",FACE,{"disambiguationData":[OSD([sQuery(id+"F0.wireOp",EDGE,"E25.0"),sQuery(id+"F0.wireOp",EDGE,"E25.1"),sQuery(id+"F0.wireOp",EDGE,"E25.2"),sQuery(id+"F0.wireOp",EDGE,"E25.3"),sQuery(id+"F0.wireOp",EDGE,"E25.4"),sQuery(id+"F0.wireOp",EDGE,"E25.5"),sQuery(id+"F0.wireOp",EDGE,"E25.6"),sQuery(id+"F0.wireOp",EDGE,"E25.7")])],"isStart":false})})});
            extrude(context, id + "F13", {"entities" : qUnion([Q0]), "operationType" : NewBodyOperationType.REMOVE, "endBound" : BoundingType.UP_TO_SURFACE, "endBoundEntityFace" : qUnion([Q1]), "depth" : 25 * mm});
        }
        {
            var Q0;
            Q0=makeQuery(id+"F3.boolean.opBoolean","COPY",EDGE,{"derivedFrom":makeQuery(id+"F3.opExtrude","CAP_EDGE",EDGE,{"disambiguationData":[OSD([sQuery(id+"F0.wireOp",EDGE,"E25.6")])],"isStart":false})});
            var Q1;
            Q1=makeQuery(id+"F8.boolean.opBoolean","INTERSECT",EDGE,{"derivedFrom":[makeQuery(id+"F5.opExtrude","SWEPT_FACE",FACE,{"disambiguationData":[OSD([sQuery(id+"F4.wireOp",EDGE,"E30")])]}),makeQuery(id+"F8.opExtrude","CAP_FACE",FACE,{"disambiguationData":[OSD([sQuery(id+"F7.wireOp",EDGE,"E67")])],"isStart":false})]});
            var Q2;
            Q2=makeQuery(id+"F8.boolean.opBoolean","INTERSECT",EDGE,{"disambiguationData":[OD(1.0)],"derivedFrom":[makeQuery(id+"F5.opExtrude","SWEPT_FACE",FACE,{"disambiguationData":[OSD([sQuery(id+"F4.wireOp",EDGE,"E30")])]}),makeQuery(id+"F8.opExtrude","SWEPT_FACE",FACE,{"disambiguationData":[OSD([sQuery(id+"F7.wireOp",EDGE,"E67")])]})]});
            var Q3;
            {var subQ0=sQuery(id+"F4.wireOp",EDGE,"E30");Q3=makeQuery(id+"F8.boolean.opBoolean","SPLIT",EDGE,{"disambiguationData":[TD([makeQuery(id+"F5.opExtrude","SWEPT_FACE",FACE,{"disambiguationData":[OSD([sQuery(id+"F4.wireOp",EDGE,"E35.filletArc")])]})])],"derivedFrom":makeQuery(id+"F5.opExtrude","CAP_EDGE",EDGE,{"disambiguationData":[OSD([subQ0])],"isStart":false})});}
            var Q4;
            {var subQ0=sQuery(id+"F0.wireOp",EDGE,"E25.7");var subQ1=sQuery(id+"F0.wireOp",EDGE,"E25.1");var subQ2=sQuery(id+"F0.wireOp",EDGE,"E25.6");var subQ3=sQuery(id+"F0.wireOp",EDGE,"E25.5");var subQ4=sQuery(id+"F0.wireOp",EDGE,"E25.4");var subQ5=sQuery(id+"F0.wireOp",EDGE,"E25.0");var subQ6=sQuery(id+"F0.wireOp",EDGE,"E25.2");var subQ7=sQuery(id+"F0.wireOp",EDGE,"E25.3");Q4=makeQuery(id+"F8.boolean.opBoolean","INTERSECT",EDGE,{"derivedFrom":[makeQuery(id+"F5.boolean.opBoolean","SPLIT",FACE,{"disambiguationData":[TD([makeQuery(id+"F2.opExtrude","SWEPT_FACE",FACE,{"disambiguationData":[OSD([subQ5])]})])],"derivedFrom":makeQuery(id+"F3.boolean.opBoolean","COPY",FACE,{"derivedFrom":makeQuery(id+"F3.opExtrude","CAP_FACE",FACE,{"disambiguationData":[OSD([subQ5,subQ1,subQ6,subQ7,subQ4,subQ3,subQ2,subQ0])],"isStart":false})})}),makeQuery(id+"F8.opExtrude","SWEPT_FACE",FACE,{"disambiguationData":[OSD([sQuery(id+"F7.wireOp",EDGE,"E67")])]})]});}
            var Q5;
            Q5=makeQuery(id+"F8.boolean.opBoolean","INTERSECT",EDGE,{"disambiguationData":[OD(0.0)],"derivedFrom":[makeQuery(id+"F5.opExtrude","SWEPT_FACE",FACE,{"disambiguationData":[OSD([sQuery(id+"F4.wireOp",EDGE,"E30")])]}),makeQuery(id+"F8.opExtrude","SWEPT_FACE",FACE,{"disambiguationData":[OSD([sQuery(id+"F7.wireOp",EDGE,"E67")])]})]});
            fillet(context, id + "F14", {"entities" : qUnion([Q0, Q1, Q2, Q3, Q4, Q5]), "radius" : 3 * mm, "tangentPropagation" : true, "allowEdgeOverflow" : false});
        }
        {
            var Q0;
            Q0=makeQuery(id+"F1.opExtrude","CAP_EDGE",EDGE,{"disambiguationData":[OSD([sQuery(id+"F0.wireOp",EDGE,"E1.bottom")])],"isStart":false});
            fillet(context, id + "F15", {"entities" : qUnion([Q0]), "radius" : 2 * mm, "tangentPropagation" : true, "allowEdgeOverflow" : false});
        }
        {
            var Q0;
            {var subQ0=sQuery(id+"F0.wireOp",EDGE,"E22.filletArc");var subQ1=sQuery(id+"F0.wireOp",EDGE,"E7");var subQ2=sQuery(id+"F0.wireOp",EDGE,"E6");var subQ3=sQuery(id+"F0.wireOp",EDGE,"E5");var subQ4=sQuery(id+"F0.wireOp",EDGE,"E4");var subQ5=sQuery(id+"F0.wireOp",EDGE,"E1.bottom");var subQ6=sQuery(id+"F0.wireOp",EDGE,"E21.filletArc");var subQ7=sQuery(id+"F0.wireOp",EDGE,"E1.top");var subQ8=sQuery(id+"F0.wireOp",EDGE,"E1.left");var subQ9=sQuery(id+"F0.wireOp",EDGE,"E1.right");var subQ10=sQuery(id+"F0.wireOp",EDGE,"E23.filletArc");var subQ11=sQuery(id+"F0.wireOp",EDGE,"E24.filletArc");Q0=makeQuery(id+"F2.boolean.opBoolean","SPLIT",FACE,{"disambiguationData":[TD([makeQuery(id+"F1.opExtrude","SWEPT_FACE",FACE,{"disambiguationData":[OSD([subQ5])]})])],"derivedFrom":makeQuery(id+"F1.opExtrude","CAP_FACE",FACE,{"disambiguationData":[OSD([subQ5,subQ7,subQ8,subQ9,subQ4,subQ3,subQ2,subQ1,subQ6,subQ0,subQ10,subQ11])],"isStart":true})});}
            var sketch = newSketch(context, id + "F16", { "sketchPlane" : qUnion([Q0])});
            skLineSegment(sketch, "E79", {"start": v(0, 74.25) * mm, "end": v(0, 104.25) * mm, "construction": true});
            skLineSegment(sketch, "E80", {"start": v(-33, 74.25) * mm, "end": v(-15, 92.25) * mm});
            skLineSegment(sketch, "E81", {"start": v(15, 92.25) * mm, "end": v(31.77, 74.25) * mm});
            skCircle(sketch, "E82", {"center": v(0, 104.25) * mm, "radius": 6 * mm});
            skLineSegment(sketch, "E83", {"start": v(-15, 92.25) * mm, "end": v(-15, 104.25) * mm});
            skArc(sketch, "E84", {"start": v(15, 104.25) * mm, "mid": v(0, 119.25) * mm, "end": v(-15, 104.25) * mm});
            skLineSegment(sketch, "E85", {"start": v(15, 104.25) * mm, "end": v(15, 92.25) * mm});
            skLineSegment(sketch, "E86", {"start": v(-74.25, 0) * mm, "end": v(74.25, 0) * mm, "construction": true});
            skArc(sketch, "E87.MirrorCS", {"start": v(15, -104.25) * mm, "mid": v(0, -119.25) * mm, "end": v(-15, -104.25) * mm});
            skLineSegment(sketch, "E88.MirrorCS", {"start": v(-15, -92.25) * mm, "end": v(-15, -104.25) * mm});
            skCircle(sketch, "E89.MirrorC", {"center": v(0, -104.25) * mm, "radius": 6 * mm});
            skLineSegment(sketch, "E90.MirrorCS", {"start": v(15, -104.25) * mm, "end": v(15, -92.25) * mm});
            skLineSegment(sketch, "E91.MirrorCS", {"start": v(15, -92.25) * mm, "end": v(31.77, -74.25) * mm});
            skLineSegment(sketch, "E92.MirrorCS", {"start": v(-33, -74.25) * mm, "end": v(-15, -92.25) * mm});
            skSolve(sketch);
        }
        {
            var Q0;
            {var subQ0=sQuery(id+"F16.wireOp",EDGE,"E80");Q0=makeQuery(id+"F16.imprint","IMPRINT",FACE,{"disambiguationData":[TD([[makeQuery(id+"F16.imprint","IMPRINT",EDGE,{"derivedFrom":subQ0}),-1.0]])]});}
            var Q1;
            Q1=makeQuery(id+"F16.imprint","IMPRINT",FACE,{"disambiguationData":[TD([[makeQuery(id+"F16.imprint","IMPRINT",EDGE,{"derivedFrom":sQuery(id+"F16.wireOp",EDGE,"E87.MirrorCS")}),-1.0]])]});
            var Q2;
            Q2=makeQuery(id+"F16.imprint","IMPRINT",FACE,{"disambiguationData":[TD([[makeQuery(id+"F16.imprint","IMPRINT",EDGE,{"derivedFrom":makeQuery(id+"F1.opExtrude","CAP_EDGE",EDGE,{"disambiguationData":[OSD([sQuery(id+"F0.wireOp",EDGE,"E1.left")])],"isStart":true})}),-1.0]])]});
            var Q3;
            Q3=makeQuery(id+"F2.opExtrude","CAP_FACE",FACE,{"disambiguationData":[OSD([sQuery(id+"F0.wireOp",EDGE,"E12"),sQuery(id+"F0.wireOp",EDGE,"E13"),sQuery(id+"F0.wireOp",EDGE,"E14"),sQuery(id+"F0.wireOp",EDGE,"E15"),sQuery(id+"F0.wireOp",EDGE,"E17.filletArc"),sQuery(id+"F0.wireOp",EDGE,"E18.filletArc"),sQuery(id+"F0.wireOp",EDGE,"E19.filletArc"),sQuery(id+"F0.wireOp",EDGE,"E20.filletArc"),sQuery(id+"F0.wireOp",EDGE,"E25.0"),sQuery(id+"F0.wireOp",EDGE,"E25.1"),sQuery(id+"F0.wireOp",EDGE,"E25.2"),sQuery(id+"F0.wireOp",EDGE,"E25.3"),sQuery(id+"F0.wireOp",EDGE,"E25.4"),sQuery(id+"F0.wireOp",EDGE,"E25.5"),sQuery(id+"F0.wireOp",EDGE,"E25.6"),sQuery(id+"F0.wireOp",EDGE,"E25.7")])],"isStart":false});
            extrude(context, id + "F17", {"entities" : qUnion([Q0, Q1, Q2]), "operationType" : NewBodyOperationType.ADD, "endBound" : BoundingType.UP_TO_SURFACE, "endBoundEntityFace" : qUnion([Q3]), "depth" : 25 * mm});
        }
    });
